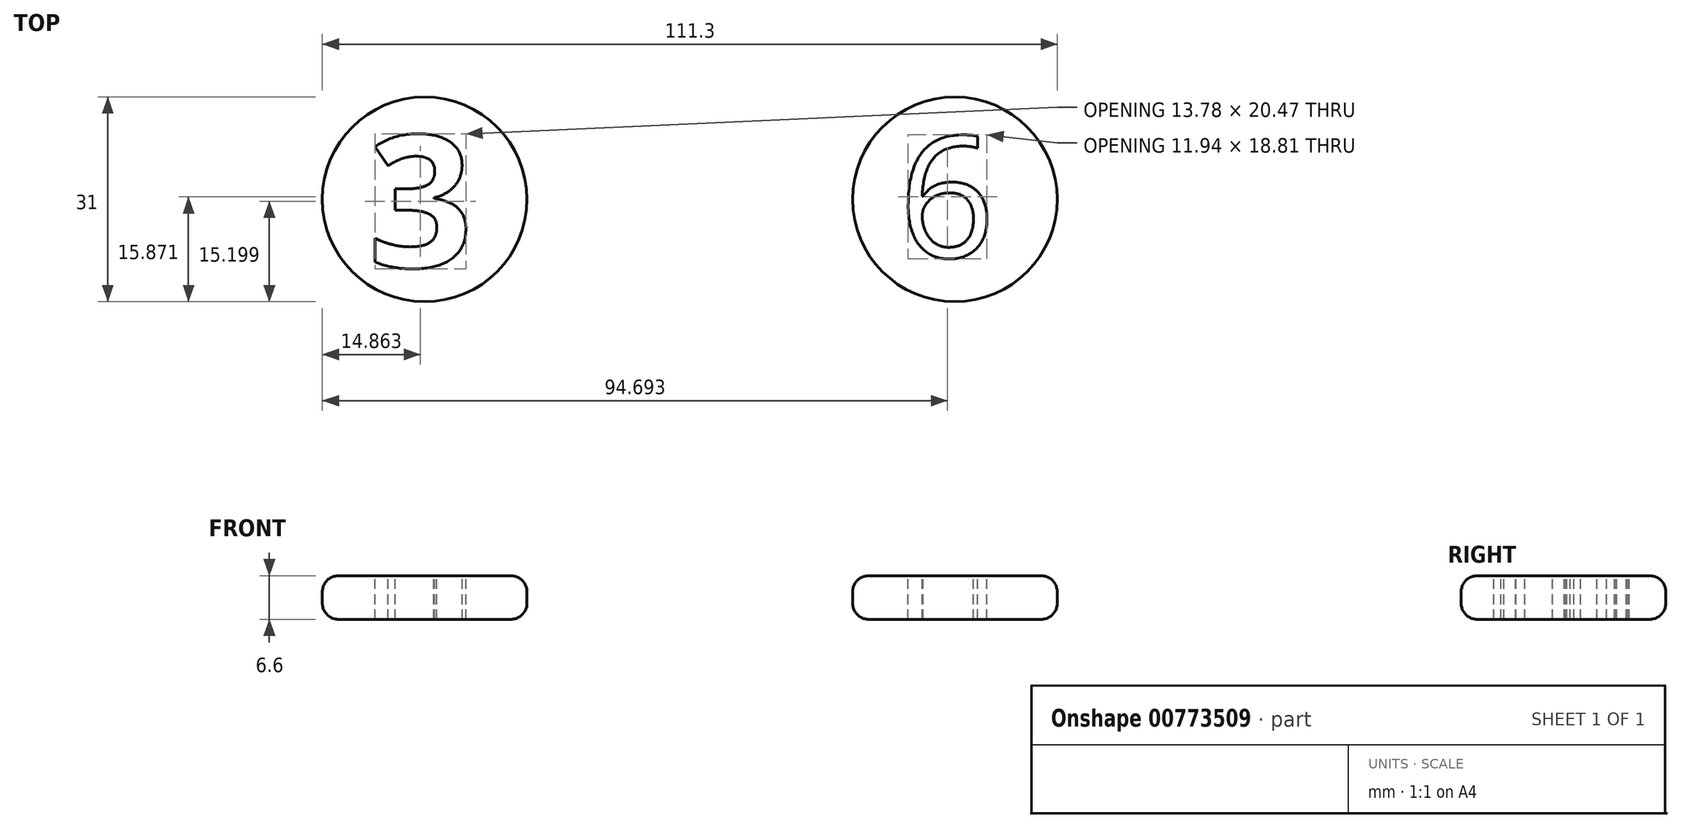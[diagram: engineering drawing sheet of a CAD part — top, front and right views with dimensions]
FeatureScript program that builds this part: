
annotation { "Feature Type Name" : "Feature", "Feature Type Description" : "" }
export const myFeature = defineFeature(function(context is Context, id is Id, definition is map)
    precondition{}
    {
        {
            var Q0;
            Q0=qCreatedBy(makeId("Top.planeOp"),FACE);
            var sketch = newSketch(context, id + "F0", { "sketchPlane" : qUnion([Q0])});
            skCircle(sketch, "E0", {"center": v(-40.15, 21.73) * mm, "radius": 15.5 * mm});
            skSolve(sketch);
        }
        {
            var Q0;
            Q0=makeQuery(id+"F0.imprint","IMPRINT",FACE,{"disambiguationData":[TD([[makeQuery(id+"F0.imprint","IMPRINT",EDGE,{"derivedFrom":sQuery(id+"F0.wireOp",EDGE,"E0")}),1.0]])]});
            extrude(context, id + "F1", {"entities" : qUnion([Q0]), "depth" : 6.6 * mm, "offsetDistance" : 25.4 * mm});
        }
        {
            var Q0;
            Q0=makeQuery(id+"F1.opExtrude","CAP_EDGE",EDGE,{"disambiguationData":[OSD([sQuery(id+"F0.wireOp",EDGE,"E0")])],"isStart":true});
            var Q1;
            Q1=makeQuery(id+"F1.opExtrude","CAP_EDGE",EDGE,{"disambiguationData":[OSD([sQuery(id+"F0.wireOp",EDGE,"E0")])],"isStart":false});
            fillet(context, id + "F2", {"entities" : qUnion([Q0, Q1]), "radius" : 2.45 * mm, "tangentPropagation" : true, "allowEdgeOverflow" : false});
        }
        {
            var Q0;
            Q0=makeQuery(id+"F1.opExtrude","SWEPT_BODY",BODY,{"disambiguationData":[OSD([sQuery(id+"F0.wireOp",EDGE,"E0")])]});
            var Q1;
            Q1=qCreatedBy(makeId("Right.planeOp"),FACE);
            mirror(context, id + "F3", {"entities" : qUnion([Q0]), "mirrorPlane" : qUnion([Q1])});
        }
        {
            var Q0;
            Q0=makeQuery(id+"F1.opExtrude","CAP_FACE",FACE,{"disambiguationData":[OSD([sQuery(id+"F0.wireOp",EDGE,"E0")])],"isStart":false});
            var sketch = newSketch(context, id + "F4", { "sketchPlane" : qUnion([Q0])});
            skText(sketch, "E1", { "text": "3", "fontName": "OpenSans-Bold.ttf"});
            const initialGuessF4  = {"E1": [-0.04874, 0.01147, 1, 0, 0.02008]};
            skSetInitialGuess(sketch, initialGuessF4);
            skSolve(sketch);
        }
        {
            var Q0;
            Q0=makeQuery(id+"F4.imprint","IMPRINT",FACE,{"disambiguationData":[TD([[makeQuery(id+"F4.imprint","IMPRINT",EDGE,{"derivedFrom":sQuery(id+"F4.wireOp",EDGE,"E1.sketch_text.stroke-0")}),-1.0]])]});
            extrude(context, id + "F5", {"entities" : qUnion([Q0]), "operationType" : NewBodyOperationType.REMOVE, "oppositeDirection" : true, "depth" : 25.4 * mm, "offsetDistance" : 25.4 * mm});
        }
        {
            var Q0;
            Q0=makeQuery(id+"F3.opPattern","COPY",FACE,{"derivedFrom":makeQuery(id+"F1.opExtrude","CAP_FACE",FACE,{"disambiguationData":[OSD([sQuery(id+"F0.wireOp",EDGE,"E0")])],"isStart":false}),"instanceName":"1"});
            var sketch = newSketch(context, id + "F6", { "sketchPlane" : qUnion([Q0])});
            skSolve(sketch);
        }
        {
            var Q0;
            {var subQ0=sQuery(id+"F0.wireOp",EDGE,"E0");Q0=makeQuery(id+"F6.imprint","IMPRINT",FACE,{"disambiguationData":[TD([[makeQuery(id+"F6.imprint","IMPRINT",EDGE,{"derivedFrom":makeQuery(id+"F3.opPattern","COPY",EDGE,{"derivedFrom":makeQuery(id+"F2.opFillet","BLEND_EDGE",EDGE,{"blendedFrom":[makeQuery(id+"F1.opExtrude","CAP_EDGE",EDGE,{"disambiguationData":[OSD([subQ0])],"isStart":false}),makeQuery(id+"F1.opExtrude","CAP_FACE",FACE,{"disambiguationData":[OSD([subQ0])],"isStart":false})],"blendedInto":[makeQuery(id+"F1.opExtrude","CAP_FACE",FACE,{"disambiguationData":[OSD([subQ0])],"isStart":false})]}),"instanceName":"1"})}),-1.0]])]});}
            var sketch = newSketch(context, id + "F7", { "sketchPlane" : qUnion([Q0])});
            skText(sketch, "E2", { "text": "6", "fontName": "OpenSans-Regular.ttf"});
            const initialGuessF7  = {"E2": [0.03161, 0.01295, 1, 0, 0.01845]};
            skSetInitialGuess(sketch, initialGuessF7);
            skSolve(sketch);
        }
        {
            var Q0;
            Q0 = qSketchRegion(id + "F7", true);
            extrude(context, id + "F8", {"entities" : qUnion([Q0]), "operationType" : NewBodyOperationType.REMOVE, "oppositeDirection" : true, "depth" : 25.4 * mm, "offsetDistance" : 25.4 * mm});
        }
    });
